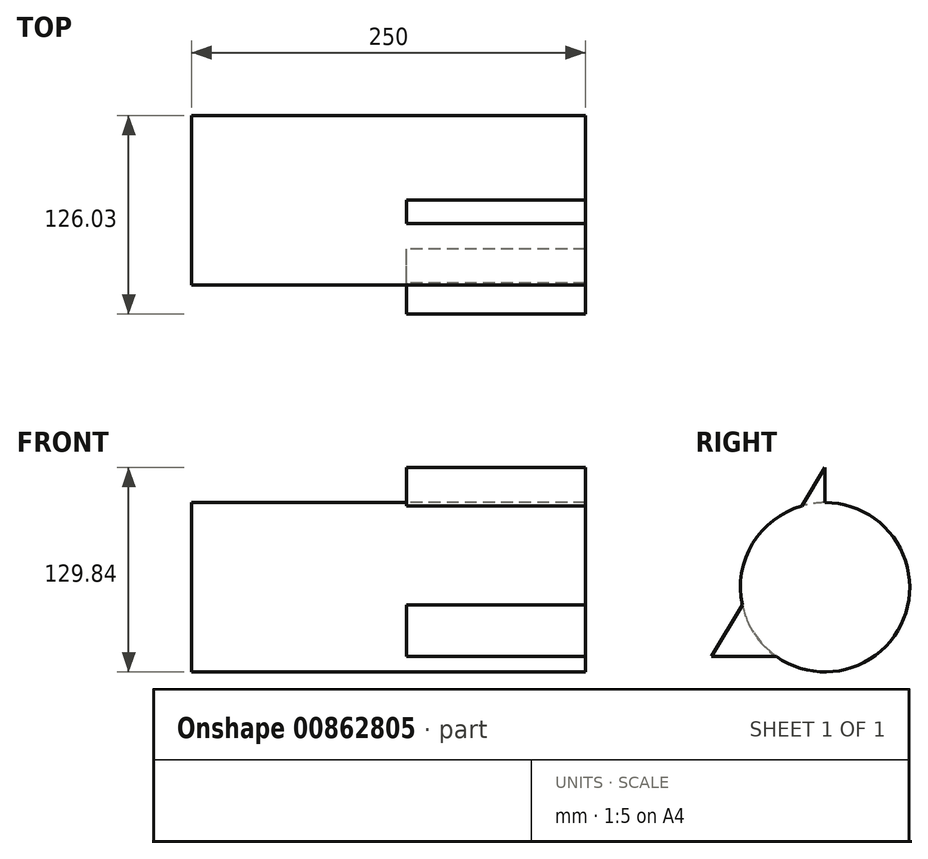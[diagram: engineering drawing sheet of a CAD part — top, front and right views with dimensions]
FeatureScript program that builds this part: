
annotation { "Feature Type Name" : "Feature", "Feature Type Description" : "" }
export const myFeature = defineFeature(function(context is Context, id is Id, definition is map)
    precondition{}
    {
        {
            var Q0;
            Q0=qCreatedBy(makeId("Right.planeOp"),FACE);
            var sketch = newSketch(context, id + "F0", { "sketchPlane" : qUnion([Q0])});
            skCircle(sketch, "E0", {"center": v(0, 0) * mm, "radius": 53.77 * mm});
            skSolve(sketch);
        }
        {
            var Q0;
            Q0=makeQuery(id+"F0.imprint","IMPRINT",FACE,{"disambiguationData":[TD([[makeQuery(id+"F0.imprint","IMPRINT",EDGE,{"derivedFrom":sQuery(id+"F0.wireOp",EDGE,"E0")}),1.0]])]});
            var Q1;
            Q1=sQuery(id+"F0.wireOp",EDGE,"E0");
            extrude(context, id + "F1", {"entities" : qUnion([Q0]), "surfaceEntities" : qUnion([Q1]), "depth" : 250 * mm, "offsetDistance" : 25 * mm});
        }
        {
            var Q0;
            Q0=makeQuery(id+"F1.opExtrude","CAP_FACE",FACE,{"disambiguationData":[OSD([sQuery(id+"F0.wireOp",EDGE,"E0")])],"isStart":false});
            var sketch = newSketch(context, id + "F2", { "sketchPlane" : qUnion([Q0])});
            skSolve(sketch);
        }
        {
            var Q0;
            Q0=makeQuery(id+"F2.imprint","IMPRINT",FACE,{"disambiguationData":[TD([[makeQuery(id+"F2.imprint","IMPRINT",EDGE,{"derivedFrom":makeQuery(id+"F1.opExtrude","CAP_EDGE",EDGE,{"disambiguationData":[OSD([sQuery(id+"F0.wireOp",EDGE,"E0")])],"isStart":false})}),1.0]])]});
            var sketch = newSketch(context, id + "F3", { "sketchPlane" : qUnion([Q0])});
            skSolve(sketch);
        }
        {
            var Q0;
            Q0=makeQuery(id+"F3.imprint","IMPRINT",FACE,{"disambiguationData":[TD([[makeQuery(id+"F3.imprint","IMPRINT",EDGE,{"derivedFrom":makeQuery(id+"F2.imprint","IMPRINT",EDGE,{"derivedFrom":makeQuery(id+"F1.opExtrude","CAP_EDGE",EDGE,{"disambiguationData":[OSD([sQuery(id+"F0.wireOp",EDGE,"E0")])],"isStart":false})})}),1.0]])]});
            var sketch = newSketch(context, id + "F4", { "sketchPlane" : qUnion([Q0])});
            skSolve(sketch);
        }
        {
            var Q0;
            Q0=makeQuery(id+"F3.imprint","IMPRINT",FACE,{"disambiguationData":[TD([[makeQuery(id+"F3.imprint","IMPRINT",EDGE,{"derivedFrom":makeQuery(id+"F2.imprint","IMPRINT",EDGE,{"derivedFrom":makeQuery(id+"F1.opExtrude","CAP_EDGE",EDGE,{"disambiguationData":[OSD([sQuery(id+"F0.wireOp",EDGE,"E0")])],"isStart":false})})}),1.0]])]});
            var sketch = newSketch(context, id + "F5", { "sketchPlane" : qUnion([Q0])});
            skLineSegment(sketch, "E1", {"start": v(0, 76.07) * mm, "end": v(-72.26, -44.01) * mm});
            skLineSegment(sketch, "E2", {"start": v(-72.26, -44.01) * mm, "end": v(0, -44.01) * mm});
            skLineSegment(sketch, "E3", {"start": v(0, -44.01) * mm, "end": v(0, 76.07) * mm});
            skSolve(sketch);
        }
        {
            var Q0;
            Q0 = qSketchRegion(id + "F5", true);
            extrude(context, id + "F6", {"entities" : qUnion([Q0]), "operationType" : NewBodyOperationType.ADD, "oppositeDirection" : true, "depth" : 113.65 * mm, "offsetDistance" : 25 * mm});
        }
    });
